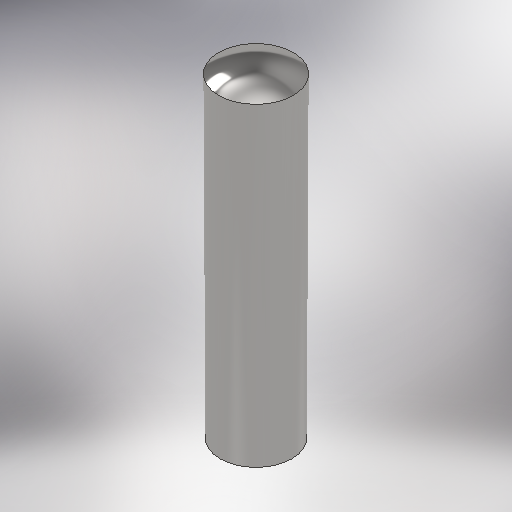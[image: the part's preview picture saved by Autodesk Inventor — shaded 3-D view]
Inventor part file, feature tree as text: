
AUTODESK INVENTOR PART (.ipt)
format: ipt  version: 2025 (Build 290162000, 162)  size: 318,976 bytes
history: native  units: mm
features: plane x2, revolve x1, sketch x1
ambient origin geometry x8: Origin, YZ Plane, XZ Plane, XY Plane, X Axis, Y Axis, Z Axis, Center Point
bodies: 实体1 (feature_tree)
feature tree (4):
  revolve  "旋转1"  [1 undecoded]
  plane  "工作平面1"
  plane  "工作平面2"
  sketch  "草图1"  dims[d0=8.5648mm d1=8.0mm d2=1.0mm d3=1.0mm d4=36.0mm d5=90.0deg d6=15.665851mm d7=11.2824mm d8=-10.7176mm d9=18.2824mm d10=17.7176mm]
note: 1 required parameter value undecoded (feature->parameter linkage not recoverable at this tier; creation-order binding heuristic only, values carry confidence <= 0.55)
